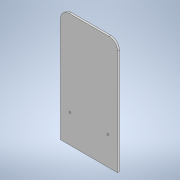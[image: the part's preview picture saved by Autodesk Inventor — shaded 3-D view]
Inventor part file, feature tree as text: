
AUTODESK INVENTOR PART (.ipt)
format: ipt  version: 2020 (Build 240168000, 168)  size: 110,592 bytes
history: native  units: in
note: dims shown in document units (in); Inventor stores cm internally (conversion verified against a paired STEP export)
features: sketch x2, extrude x1, fillet x1, hole x1
ambient origin geometry x8: Origin, YZ Plane, XZ Plane, XY Plane, X Axis, Y Axis, Z Axis, Center Point
bodies: Solid1 (feature_tree)
feature tree (5):
  extrude  "Extrusion1"  Depth=11.811in
  fillet  "Fillet1"  Radius=5.9055in
  hole  "Hole1"  [1 undecoded]
  sketch  "Sketch1"  dims[d0=23.622in d1=11.811in d2=5.9055in]
  sketch  "Sketch2"  dims[d3=0.3937in d4=0.0in d5=1.7717in d6=1.9685in d7=1.9685in d8=5.9055in d9=5.9055in d10=0.315in d11=0.2362in d12=0.5512in d13=0.2756in d14=90.0deg d15=2.3622in d16=0.0in]
note: 1 required parameter value undecoded (feature->parameter linkage not recoverable at this tier; creation-order binding heuristic only, values carry confidence <= 0.55)
